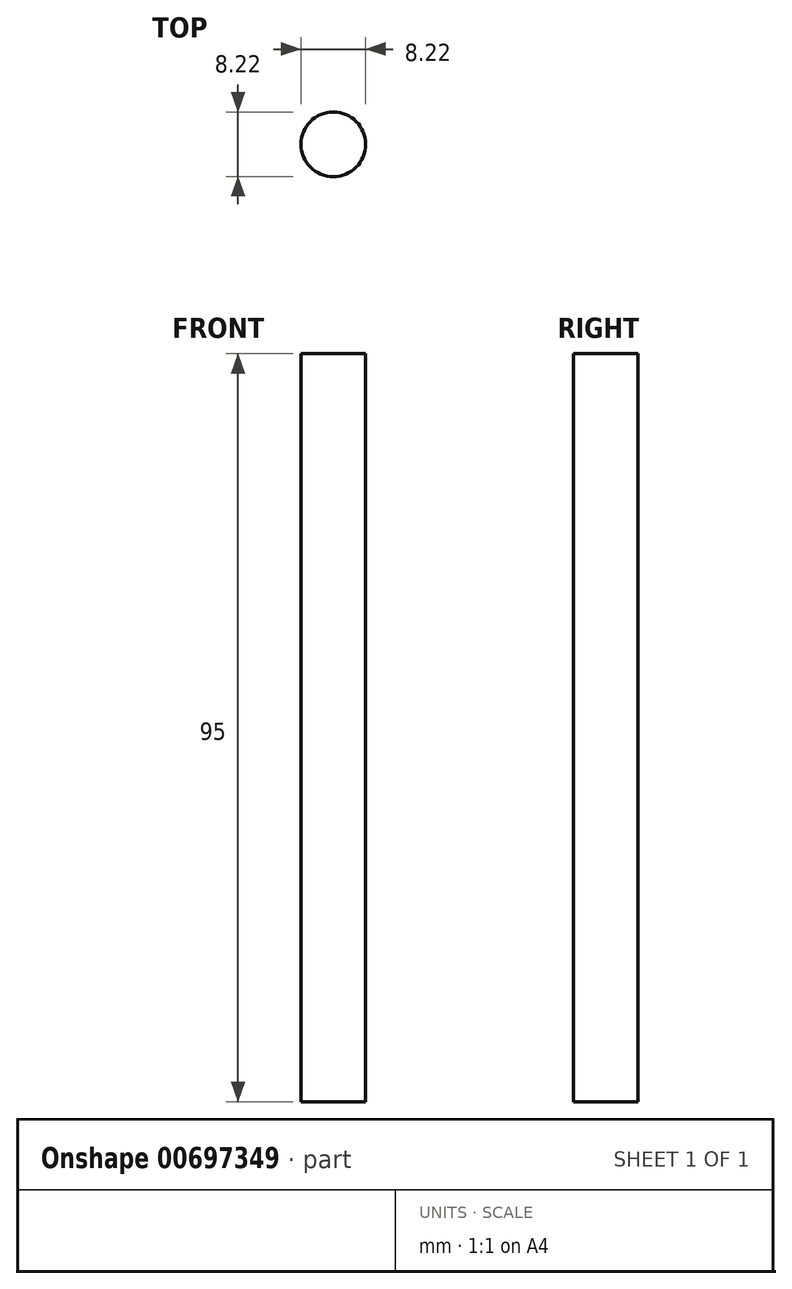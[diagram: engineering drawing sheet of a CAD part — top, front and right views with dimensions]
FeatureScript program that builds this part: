
annotation { "Feature Type Name" : "Feature", "Feature Type Description" : "" }
export const myFeature = defineFeature(function(context is Context, id is Id, definition is map)
    precondition{}
    {
        {
            var Q0;
            Q0=qCreatedBy(makeId("Top.planeOp"),FACE);
            var sketch = newSketch(context, id + "F0", { "sketchPlane" : qUnion([Q0])});
            skCircle(sketch, "E0", {"center": v(0, 0) * mm, "radius": 4.11 * mm});
            skSolve(sketch);
        }
        {
            var Q0;
            Q0 = qSketchRegion(id + "F0", true);
            extrude(context, id + "F1", {"entities" : qUnion([Q0]), "depth" : 95 * mm, "offsetDistance" : 25 * mm});
        }
    });
